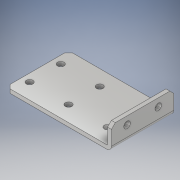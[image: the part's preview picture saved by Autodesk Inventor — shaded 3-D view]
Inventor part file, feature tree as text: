
AUTODESK INVENTOR PART (.ipt)
format: ipt  version: 2017.1 (Build 211199000, 199)  size: 127,488 bytes
history: native  units: in
note: dims shown in document units (in); Inventor stores cm internally (conversion verified against a paired STEP export)
features: chamfer x1
ambient origin geometry x8: Origin, YZ Plane, XZ Plane, XY Plane, X Axis, Y Axis, Z Axis, Center Point
bodies: Solid1 (feature_tree)
feature tree (1):
  chamfer  "Chamfer2"  [1 undecoded]
note: 1 required parameter value undecoded (feature->parameter linkage not recoverable at this tier; creation-order binding heuristic only, values carry confidence <= 0.55)
